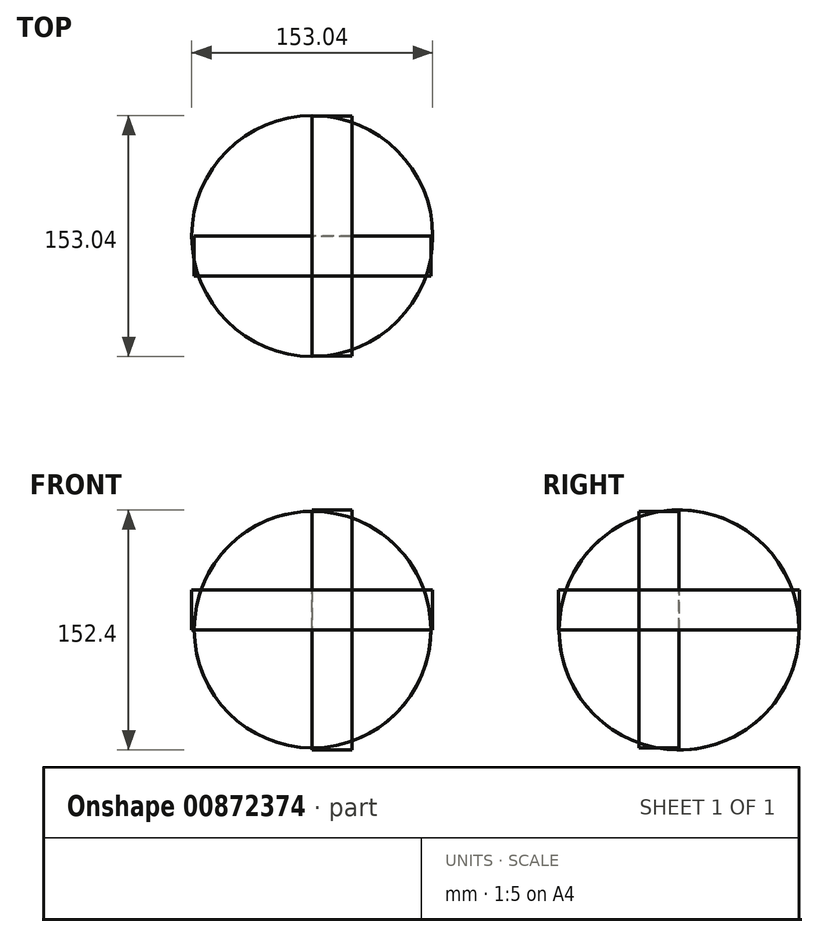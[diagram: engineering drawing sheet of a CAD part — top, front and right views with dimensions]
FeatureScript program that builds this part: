
annotation { "Feature Type Name" : "Feature", "Feature Type Description" : "" }
export const myFeature = defineFeature(function(context is Context, id is Id, definition is map)
    precondition{}
    {
        {
            var Q0;
            Q0=qCreatedBy(makeId("Front.planeOp"),FACE);
            var sketch = newSketch(context, id + "F0", { "sketchPlane" : qUnion([Q0])});
            skCircle(sketch, "E0", {"center": v(0.17, 0.22) * mm, "radius": 75.13 * mm});
            skSolve(sketch);
        }
        {
            var Q0;
            Q0=qCreatedBy(makeId("Right.planeOp"),FACE);
            var sketch = newSketch(context, id + "F1", { "sketchPlane" : qUnion([Q0])});
            skCircle(sketch, "E1", {"center": v(0, 0) * mm, "radius": 76.2 * mm});
            skSolve(sketch);
        }
        {
            var Q0;
            Q0=qCreatedBy(makeId("Top.planeOp"),FACE);
            var sketch = newSketch(context, id + "F2", { "sketchPlane" : qUnion([Q0])});
            skCircle(sketch, "E2", {"center": v(0, 0) * mm, "radius": 76.52 * mm});
            skSolve(sketch);
        }
        {
            var Q0;
            Q0=sQuery(id+"F0.wireOp",EDGE,"E0");
            extrude(context, id + "F3", {"bodyType" : ToolBodyType.SURFACE, "surfaceEntities" : qUnion([Q0]), "depth" : 25.4 * mm, "offsetDistance" : 25.4 * mm});
        }
        {
            var Q0;
            Q0=sQuery(id+"F2.wireOp",EDGE,"E2");
            extrude(context, id + "F4", {"bodyType" : ToolBodyType.SURFACE, "surfaceEntities" : qUnion([Q0]), "depth" : 25.4 * mm, "offsetDistance" : 25.4 * mm});
        }
        {
            var Q0;
            Q0=sQuery(id+"F1.wireOp",EDGE,"E1");
            extrude(context, id + "F5", {"bodyType" : ToolBodyType.SURFACE, "surfaceEntities" : qUnion([Q0]), "depth" : 25.4 * mm, "offsetDistance" : 25.4 * mm});
        }
    });
